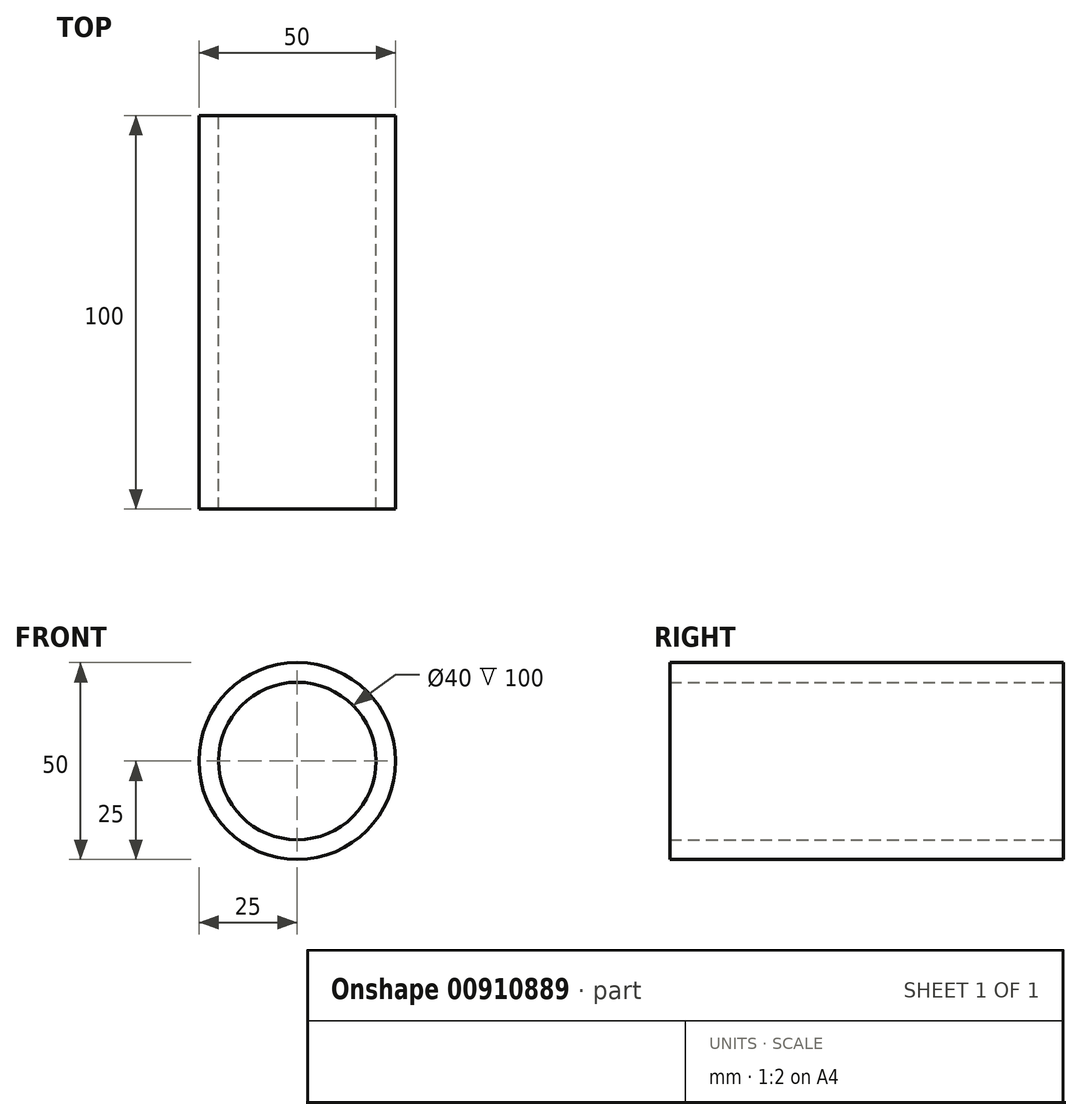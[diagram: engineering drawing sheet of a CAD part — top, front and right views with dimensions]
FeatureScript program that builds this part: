
annotation { "Feature Type Name" : "Feature", "Feature Type Description" : "" }
export const myFeature = defineFeature(function(context is Context, id is Id, definition is map)
    precondition{}
    {
        {
            var Q0;
            Q0=qCreatedBy(makeId("Front.planeOp"),FACE);
            var sketch = newSketch(context, id + "F0", { "sketchPlane" : qUnion([Q0])});
            skCircle(sketch, "E0", {"center": v(0, 0) * mm, "radius": 25 * mm});
            skCircle(sketch, "E1", {"center": v(0, 0) * mm, "radius": 20 * mm});
            skSolve(sketch);
        }
        {
            var Q0;
            Q0=makeQuery(id+"F0.imprint","IMPRINT",FACE,{"disambiguationData":[TD([[makeQuery(id+"F0.imprint","IMPRINT",EDGE,{"derivedFrom":sQuery(id+"F0.wireOp",EDGE,"E0")}),1.0]])]});
            extrude(context, id + "F1", {"entities" : qUnion([Q0]), "depth" : 100 * mm, "offsetDistance" : 25 * mm});
        }
    });
